# Revit family: BS 5EN
name_source: partatom
category: Dispositivi di comunicazione
units: mm (PartAtom-declared; Revit-internal decimal feet)

## family parameters
Condiviso = Sì
Host = Superficie
Mantenere orientamento annotazione = No
Numero OmniClass = 23.85.10.11.11.21
Punto di calcolo locali = No
Quota connettore circolare = Usa diametro
Taglio con vuoti quando caricato = No
Tipo di parte = Normale
Titolo OmniClass = Speakers

## types (1)
- BS 5EN
    CE marking = Yes
    CPR number = 0068-CPR-058/2014
    Cabinet/Case Material = ABS
    Color = White - RAL 9016
    Constant Voltage Transformer = 100 V
    Data Sheet = https://www.rcf.it
    Depth = 183 mm / 7.2 inches
    Descrizione = BS 5EN is a 20 W suspended sound projector in compliance with EN 54-24:2008 regulations.
It is suitable for all those installations where high intelligibility for alarm messages broadcasting and great sound reproduction quality are required. Its 5’’ coaxial transducer guarantees an excellent coverage and sound uniformity, optimizing the number of speakers needed.
A modern and endearing design makes it the perfect product for environments where projectors are intended also as architectural elements and contribute to improve global aesthetics.
    EN54-24 certified = Yes
    Frequency Response (-10dB) = 80 Hz ÷ 20000 Hz
    Grille = Steel
    Hardware = 5m cable
    Height = 261 mm / 10.28 inches
    Horizontal coverage angle = 170°
    IP protection grade = IP 65
    Input/Output section = Ceramic screw terminals
    Max SPL @ 1m = 101 dB
    Max SPL @ 4m = 89 dB
    Modello = BS 5EN
    Output connectors = Ceramic screw terminals
    Part Numbers = 13133078
    Peak Power Handling = 80 W PEAK
    Power Handling = 20 W RMS
    Power selection 1 (100 V) = 20 W - 500 ohm
    Power selection 2 (100 V) = 10 W - 1000 ohm
    Power selection 3 (100 V) = 5 W - 2000 ohm
    Power selection 4 (100 V) = 2.5 W - 4000 ohm
    Prospetto di default = 1000 mm  [stored 3.28084 ft]
    Protections = Thermal fuse
    Recommended Amplifier = 40 W
    System Sensitivity = 88 dB
    System Sensitivity 1W @ 4m = 76 dB
    URL = http://www.rcf.it
    Vertical coverage angle = 170°
    Weight = 2.79 kg / 6.15 lbs
    Width = 176 mm / 6.93 inches

note: [stored X ft] marks values corroborated as IEEE doubles in the binary element streams (Revit-internal decimal feet)
